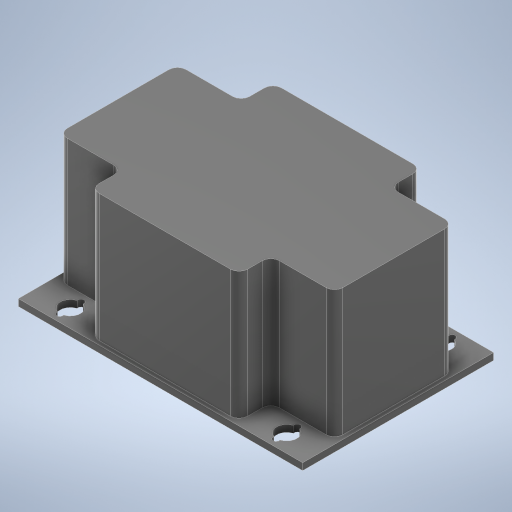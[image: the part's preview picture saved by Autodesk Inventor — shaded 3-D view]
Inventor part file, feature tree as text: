
AUTODESK INVENTOR PART (.ipt)
format: ipt  version: 2024.2 (Build 282272000, 272)  size: 311,296 bytes
history: native  units: mm
features: extrude x2, sketch x1, fillet x1
ambient origin geometry x8: Origin, YZ Plane, XZ Plane, XY Plane, X Axis, Y Axis, Z Axis, Center Point
bodies: Solid1 (feature_tree)
feature tree (4):
  sketch  "Sketch1"  dims[d0=45.0mm d1=67.0mm d7=1.6mm d8=0.0mm d9=31.6mm d10=0.0mm d18=2.0mm d19=4.8mm d33=51.0mm d34=36.5mm d38=1.0mm d43=1.0mm d44=1.0mm d46=6.5mm d47=1.5mm d48=1.0mm d50=16.0mm]
  extrude  "Extrusion1"  Depth=67.0mm
  extrude  "Extrusion2"  Depth=1.6mm TaperAngle=0.0deg
  fillet  "Fillet1"  Radius=31.6mm
